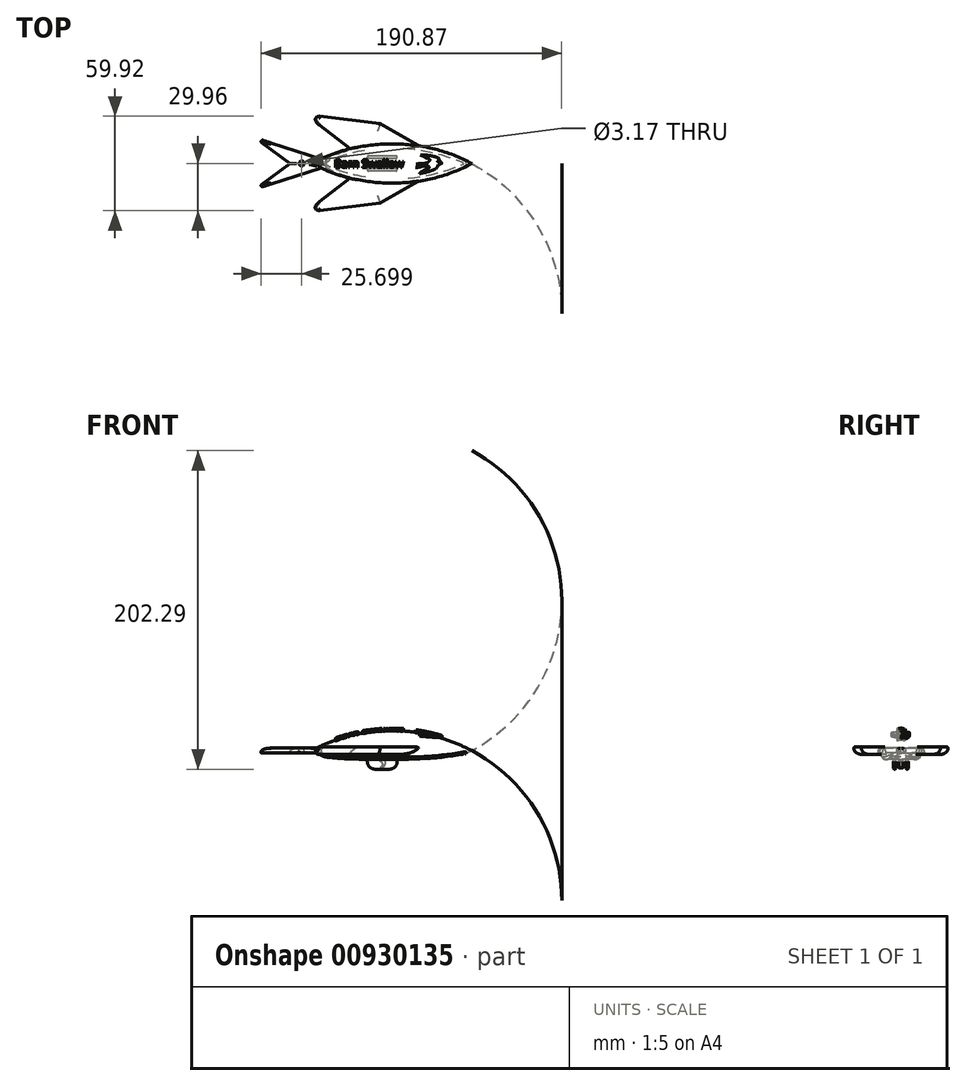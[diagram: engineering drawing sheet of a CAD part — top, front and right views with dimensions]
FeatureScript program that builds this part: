
annotation { "Feature Type Name" : "Feature", "Feature Type Description" : "" }
export const myFeature = defineFeature(function(context is Context, id is Id, definition is map)
    precondition{}
    {
        {
            var Q0;
            Q0=qCreatedBy(makeId("Top.planeOp"),FACE);
            var sketch = newSketch(context, id + "F0", { "sketchPlane" : qUnion([Q0])});
            skArc(sketch, "E0", {"start": v(50.5, 0) * mm, "mid": v(-0.3, 12.7) * mm, "end": v(-51.1, 0) * mm});
            skLineSegment(sketch, "E1", {"start": v(-51.1, 0) * mm, "end": v(50.5, 0) * mm});
            skSolve(sketch);
        }
        {
            var Q0;
            Q0 = qSketchRegion(id + "F0", true);
            var Q1;
            Q1=sQuery(id+"F0.wireOp",EDGE,"E1");
            revolve(context, id + "F1", {"surfaceOperationType" : NewSurfaceOperationType.NEW, "entities" : qUnion([Q0]), "axis" : qUnion([Q1]), "revolveType" : RevolveType.FULL});
        }
        {
            var Q0;
            Q0=qCreatedBy(makeId("Top.planeOp"),FACE);
            var sketch = newSketch(context, id + "F2", { "sketchPlane" : qUnion([Q0])});
            skLineSegment(sketch, "E2", {"start": v(25.4, 6.35) * mm, "end": v(-7.66, 25.44) * mm});
            skLineSegment(sketch, "E3", {"start": v(-7.66, 25.44) * mm, "end": v(-58.1, 31.57) * mm});
            skLineSegment(sketch, "E4", {"start": v(-25.4, 6.35) * mm, "end": v(25.4, 6.35) * mm});
            skPoint(sketch, "E5.visualSharp", {"position": v(-7.66, 25.44) * mm});
            skLineSegment(sketch, "E6", {"start": v(-12.7, 0) * mm, "end": v(12.7, 0) * mm, "construction": true});
            skLineSegment(sketch, "E7.MirrorCS", {"start": v(-7.66, -25.44) * mm, "end": v(-7.66, -25.44) * mm});
            skPoint(sketch, "E8.MirrorP", {"position": v(-7.66, -25.44) * mm});
            skLineSegment(sketch, "E9.MirrorCS", {"start": v(-25.4, -6.35) * mm, "end": v(25.4, -6.35) * mm});
            skLineSegment(sketch, "E10.MirrorCS", {"start": v(-7.66, -25.44) * mm, "end": v(-58.1, -31.57) * mm});
            skLineSegment(sketch, "E11.MirrorCS", {"start": v(25.4, -6.35) * mm, "end": v(-7.66, -25.44) * mm});
            skLineSegment(sketch, "E12", {"start": v(-25.4, 6.35) * mm, "end": v(-58.1, 31.57) * mm});
            skLineSegment(sketch, "E13", {"start": v(-58.1, -31.57) * mm, "end": v(-25.4, -6.35) * mm});
            skSolve(sketch);
        }
        {
            var Q0;
            Q0 = qSketchRegion(id + "F2", true);
            extrude(context, id + "F3", {"entities" : qUnion([Q0]), "operationType" : NewBodyOperationType.ADD, "depth" : 4.7 * mm, "offsetDistance" : 25.4 * mm, "symmetric" : true});
        }
        {
            var Q0;
            Q0=qCreatedBy(makeId("Front.planeOp"),FACE);
            var sketch = newSketch(context, id + "F4", { "sketchPlane" : qUnion([Q0])});
            skLineSegment(sketch, "E14", {"start": v(-65.9, -0.5) * mm, "end": v(22.2, 2.57) * mm});
            skLineSegment(sketch, "E15", {"start": v(22.2, 2.57) * mm, "end": v(19.39, 14.95) * mm});
            skLineSegment(sketch, "E16", {"start": v(19.39, 14.95) * mm, "end": v(-60.79, 12.82) * mm});
            skLineSegment(sketch, "E17", {"start": v(-60.79, 12.82) * mm, "end": v(-65.9, -0.5) * mm});
            skLineSegment(sketch, "E18", {"start": v(13.47, 0) * mm, "end": v(-58.08, 0) * mm, "construction": true});
            skSolve(sketch);
        }
        {
            var Q0;
            Q0=makeQuery(id+"F3.opExtrude","CAP_EDGE",EDGE,{"disambiguationData":[OSD([sQuery(id+"F2.wireOp",EDGE,"E2")])],"isStart":true});
            var Q1;
            Q1=makeQuery(id+"F3.opExtrude","CAP_EDGE",EDGE,{"disambiguationData":[OSD([sQuery(id+"F2.wireOp",EDGE,"E3")])],"isStart":true});
            var Q2;
            Q2=makeQuery(id+"F3.opExtrude","CAP_EDGE",EDGE,{"disambiguationData":[OSD([sQuery(id+"F2.wireOp",EDGE,"E11.MirrorCS")])],"isStart":true});
            var Q3;
            Q3=makeQuery(id+"F3.opExtrude","CAP_EDGE",EDGE,{"disambiguationData":[OSD([sQuery(id+"F2.wireOp",EDGE,"E10.MirrorCS")])],"isStart":true});
            fillet(context, id + "F5", {"entities" : qUnion([Q0, Q1, Q2, Q3]), "radius" : 5.08 * mm, "tangentPropagation" : true, "allowEdgeOverflow" : false});
        }
        {
            var Q0;
            Q0=makeQuery(id+"F3.opExtrude","CAP_EDGE",EDGE,{"disambiguationData":[OSD([sQuery(id+"F2.wireOp",EDGE,"E12")])],"isStart":false});
            var Q1;
            Q1=makeQuery(id+"F3.opExtrude","CAP_EDGE",EDGE,{"disambiguationData":[OSD([sQuery(id+"F2.wireOp",EDGE,"E13")])],"isStart":false});
            chamfer(context, id + "F6", {"entities" : qUnion([Q0, Q1]), "width" : 5.08 * mm, "tangentPropagation" : true});
        }
        {
            var Q0;
            Q0=qCreatedBy(makeId("Front.planeOp"),FACE);
            var sketch = newSketch(context, id + "F7", { "sketchPlane" : qUnion([Q0])});
            skLineSegment(sketch, "E19", {"start": v(6.9, -5.44) * mm, "end": v(-17.13, -5.44) * mm});
            skLineSegment(sketch, "E20", {"start": v(54.85, -5.44) * mm, "end": v(0, -26.45) * mm});
            skLineSegment(sketch, "E21", {"start": v(0, -26.45) * mm, "end": v(-69.23, -5.44) * mm});
            skLineSegment(sketch, "E22", {"start": v(58.81, 0) * mm, "end": v(73.58, 4.5) * mm});
            skLineSegment(sketch, "E23", {"start": v(58.81, 0) * mm, "end": v(54.85, -5.44) * mm});
            skLineSegment(sketch, "E24", {"start": v(-63.97, -0.59) * mm, "end": v(-66.78, 0) * mm});
            skLineSegment(sketch, "E25", {"start": v(-66.78, 0) * mm, "end": v(-69.23, -5.44) * mm});
            skPoint(sketch, "E26.visualSharp", {"position": v(40.98, -5.44) * mm});
            skArc(sketch, "E26.filletArc", {"start": v(6.9, -5.44) * mm, "mid": v(40.6, -2.94) * mm, "end": v(73.58, 4.5) * mm});
            skPoint(sketch, "E27.visualSharp", {"position": v(-40.8, -5.44) * mm});
            skArc(sketch, "E27.filletArc", {"start": v(-63.97, -0.59) * mm, "mid": v(-40.67, -4.22) * mm, "end": v(-17.13, -5.44) * mm});
            skSolve(sketch);
        }
        {
            var Q0;
            Q0 = qSketchRegion(id + "F7", true);
            extrude(context, id + "F8", {"entities" : qUnion([Q0]), "operationType" : NewBodyOperationType.REMOVE, "oppositeDirection" : true, "depth" : 25.4 * mm, "offsetDistance" : 25.4 * mm, "symmetric" : true});
        }
        {
            var Q0;
            Q0=makeQuery(id+"F8.boolean.opBoolean","INTERSECT",EDGE,{"derivedFrom":[makeQuery(id+"F1.opRevolve","SWEPT_FACE",FACE,{"disambiguationData":[OSD([sQuery(id+"F0.wireOp",EDGE,"E0")])]}),makeQuery(id+"F8.opExtrude","SWEPT_FACE",FACE,{"disambiguationData":[OSD([sQuery(id+"F7.wireOp",EDGE,"E19")])]})]});
            fillet(context, id + "F9", {"entities" : qUnion([Q0]), "radius" : 2.03 * mm, "tangentPropagation" : true, "allowEdgeOverflow" : false});
        }
        {
            var Q0;
            Q0=qCreatedBy(makeId("Top.planeOp"),FACE);
            var sketch = newSketch(context, id + "F10", { "sketchPlane" : qUnion([Q0])});
            skLineSegment(sketch, "E28", {"start": v(-36.1, 0) * mm, "end": v(-86.74, 16.16) * mm});
            skLineSegment(sketch, "E29", {"start": v(-86.74, 16.16) * mm, "end": v(-64.97, 0) * mm});
            skLineSegment(sketch, "E30", {"start": v(-64.97, 0) * mm, "end": v(-36.1, 0) * mm});
            skLineSegment(sketch, "E31.MirrorCS", {"start": v(-86.74, -16.16) * mm, "end": v(-64.97, 0) * mm});
            skLineSegment(sketch, "E32.MirrorCS", {"start": v(-36.1, 0) * mm, "end": v(-86.74, -16.16) * mm});
            skSolve(sketch);
        }
        {
            var Q0;
            Q0 = qSketchRegion(id + "F10", true);
            extrude(context, id + "F11", {"entities" : qUnion([Q0]), "operationType" : NewBodyOperationType.ADD, "depth" : 3.17 * mm, "offsetDistance" : 25.4 * mm, "symmetric" : true});
        }
        {
            var Q0;
            Q0=makeQuery(id+"F11.opExtrude","CAP_EDGE",EDGE,{"disambiguationData":[OSD([sQuery(id+"F10.wireOp",EDGE,"E29")])],"isStart":false});
            var Q1;
            Q1=makeQuery(id+"F11.opExtrude","CAP_EDGE",EDGE,{"disambiguationData":[OSD([sQuery(id+"F10.wireOp",EDGE,"E31.MirrorCS")])],"isStart":false});
            fillet(context, id + "F12", {"entities" : qUnion([Q0, Q1]), "radius" : 2.54 * mm, "tangentPropagation" : true, "allowEdgeOverflow" : false});
        }
        {
            var Q0;
            Q0=makeQuery(id+"F8.boolean.opBoolean","COPY",FACE,{"derivedFrom":makeQuery(id+"F8.opExtrude","SWEPT_FACE",FACE,{"disambiguationData":[OSD([sQuery(id+"F7.wireOp",EDGE,"E19")])]})});
            var sketch = newSketch(context, id + "F13", { "sketchPlane" : qUnion([Q0])});
            skLineSegment(sketch, "E33", {"start": v(6.9, 9.85) * mm, "end": v(-17.13, -8.68) * mm, "construction": true});
            skLineSegment(sketch, "E34", {"start": v(-17.13, 8.68) * mm, "end": v(6.9, -9.85) * mm, "construction": true});
            skLineSegment(sketch, "E35.bottom", {"start": v(-4.17, 1.32) * mm, "end": v(-7.59, 1.32) * mm});
            skLineSegment(sketch, "E35.top", {"start": v(-4.17, -1.32) * mm, "end": v(-7.59, -1.32) * mm});
            skLineSegment(sketch, "E35.left", {"start": v(-4.17, 1.32) * mm, "end": v(-4.17, -1.32) * mm});
            skLineSegment(sketch, "E35.right", {"start": v(-7.59, 1.32) * mm, "end": v(-7.59, -1.32) * mm});
            skPoint(sketch, "E35.middle", {"position": v(-5.88, 0) * mm});
            skSolve(sketch);
        }
        {
            var Q0;
            Q0=makeQuery(id+"F13.imprint","IMPRINT",FACE,{"disambiguationData":[TD([[makeQuery(id+"F13.imprint","IMPRINT",EDGE,{"derivedFrom":sQuery(id+"F13.wireOp",EDGE,"E35.bottom")}),1.0]])]});
            var Q1;
            Q1=sQuery(id+"F13.wireOp",EDGE,"E35.right");
            var Q2;
            Q2=sQuery(id+"F13.wireOp",EDGE,"E35.bottom");
            var Q3;
            Q3=sQuery(id+"F13.wireOp",EDGE,"E35.left");
            var Q4;
            Q4=sQuery(id+"F13.wireOp",EDGE,"E35.top");
            extrude(context, id + "F14", {"entities" : qUnion([Q0]), "operationType" : NewBodyOperationType.ADD, "surfaceEntities" : qUnion([Q1, Q2, Q3, Q4]), "depth" : 6.35 * mm, "offsetDistance" : 25.4 * mm});
        }
        {
            var Q0;
            Q0=makeQuery(id+"F14.opExtrude","SWEPT_FACE",FACE,{"disambiguationData":[OSD([sQuery(id+"F13.wireOp",EDGE,"E35.bottom")])]});
            var sketch = newSketch(context, id + "F15", { "sketchPlane" : qUnion([Q0])});
            skCircle(sketch, "E36", {"center": v(-7.59, -8.61) * mm, "radius": 1.59 * mm});
            skSolve(sketch);
        }
        {
            var Q0;
            {var subQ0=sQuery(id+"F15.wireOp",EDGE,"E36");var subQ1=makeQuery(id+"F14.opExtrude","SWEPT_EDGE",EDGE,{"disambiguationData":[OSD([sQuery(id+"F13.wireOp",EDGE,"E35.bottom"),sQuery(id+"F13.wireOp",EDGE,"E35.right")])]});var subQ2=makeQuery(id+"F15.imprint","INTERSECT",VERTEX,{"disambiguationData":[OD(0.0)],"derivedFrom":[subQ1,subQ0]});Q0=makeQuery(id+"F15.imprint","IMPRINT",FACE,{"disambiguationData":[TD([[makeQuery(id+"F15.imprint","IMPRINT",EDGE,{"disambiguationData":[TD([[subQ2,-1.0]])],"derivedFrom":subQ0}),1.0]])]});}
            extrude(context, id + "F16", {"entities" : qUnion([Q0]), "operationType" : NewBodyOperationType.REMOVE, "oppositeDirection" : true, "depth" : 25.4 * mm, "offsetDistance" : 25.4 * mm, "symmetric" : true});
        }
        {
            var Q0;
            Q0=makeQuery(id+"F14.opExtrude","CAP_EDGE",EDGE,{"disambiguationData":[OSD([sQuery(id+"F13.wireOp",EDGE,"E35.left")])],"isStart":false});
            fillet(context, id + "F17", {"entities" : qUnion([Q0]), "radius" : 5.08 * mm, "tangentPropagation" : true, "allowEdgeOverflow" : false});
        }
        {
            var Q0;
            {var subQ0=sQuery(id+"F13.wireOp",EDGE,"E35.bottom");var subQ1=sQuery(id+"F13.wireOp",EDGE,"E35.right");var subQ2=sQuery(id+"F13.wireOp",EDGE,"E35.left");var subQ3=sQuery(id+"F13.wireOp",EDGE,"E35.top");Q0=makeQuery(id+"F17.opFillet","BLEND_EDGE",EDGE,{"blendedFrom":[makeQuery(id+"F14.opExtrude","CAP_EDGE",EDGE,{"disambiguationData":[OSD([subQ2])],"isStart":false}),makeQuery(id+"F16.boolean.opBoolean","SPLIT",FACE,{"disambiguationData":[TD([makeQuery(id+"F14.opExtrude","CAP_FACE",FACE,{"disambiguationData":[OSD([subQ0,subQ3,subQ2,subQ1])],"isStart":false})])],"derivedFrom":makeQuery(id+"F14.opExtrude","SWEPT_FACE",FACE,{"disambiguationData":[OSD([subQ1])]})})],"blendedInto":[makeQuery(id+"F16.boolean.opBoolean","SPLIT",FACE,{"disambiguationData":[TD([makeQuery(id+"F14.opExtrude","CAP_FACE",FACE,{"disambiguationData":[OSD([subQ0,subQ3,subQ2,subQ1])],"isStart":false})])],"derivedFrom":makeQuery(id+"F14.opExtrude","SWEPT_FACE",FACE,{"disambiguationData":[OSD([subQ1])]})})]});}
            fillet(context, id + "F18", {"entities" : qUnion([Q0]), "radius" : 1.27 * mm, "tangentPropagation" : true, "allowEdgeOverflow" : false});
        }
        {
            var Q0;
            Q0=makeQuery(id+"F11.opExtrude","CAP_FACE",FACE,{"disambiguationData":[OSD([sQuery(id+"F10.wireOp",EDGE,"E28"),sQuery(id+"F10.wireOp",EDGE,"E29"),sQuery(id+"F10.wireOp",EDGE,"E31.MirrorCS"),sQuery(id+"F10.wireOp",EDGE,"E32.MirrorCS")])],"isStart":false});
            var sketch = newSketch(context, id + "F19", { "sketchPlane" : qUnion([Q0])});
            skCircle(sketch, "E37", {"center": v(-57.53, 0) * mm, "radius": 1.59 * mm});
            skSolve(sketch);
        }
        {
            var Q0;
            Q0 = qSketchRegion(id + "F19", true);
            extrude(context, id + "F20", {"entities" : qUnion([Q0]), "operationType" : NewBodyOperationType.REMOVE, "oppositeDirection" : true, "depth" : 25.4 * mm, "offsetDistance" : 25.4 * mm});
        }
        {
            var Q0;
            Q0=makeQuery(id+"F20.boolean.opBoolean","COPY",EDGE,{"derivedFrom":makeQuery(id+"F20.opExtrude","CAP_EDGE",EDGE,{"disambiguationData":[OSD([sQuery(id+"F19.wireOp",EDGE,"E37")])],"isStart":true})});
            var Q1;
            Q1=makeQuery(id+"F20.boolean.opBoolean","INTERSECT",EDGE,{"derivedFrom":[makeQuery(id+"F11.opExtrude","CAP_FACE",FACE,{"disambiguationData":[OSD([sQuery(id+"F10.wireOp",EDGE,"E28"),sQuery(id+"F10.wireOp",EDGE,"E29"),sQuery(id+"F10.wireOp",EDGE,"E31.MirrorCS"),sQuery(id+"F10.wireOp",EDGE,"E32.MirrorCS")])],"isStart":true}),makeQuery(id+"F20.opExtrude","SWEPT_FACE",FACE,{"disambiguationData":[OSD([sQuery(id+"F19.wireOp",EDGE,"E37")])]})]});
            fillet(context, id + "F21", {"entities" : qUnion([Q0, Q1]), "radius" : 1.27 * mm, "tangentPropagation" : true, "allowEdgeOverflow" : false});
        }
        {
            var Q0;
            Q0=qCreatedBy(makeId("Top.planeOp"),FACE);
            var sketch = newSketch(context, id + "F22", { "sketchPlane" : qUnion([Q0])});
            skArc(sketch, "E38", {"start": v(28.55, 3.87) * mm, "mid": v(23.4, 5.07) * mm, "end": v(18.1, 5.23) * mm});
            skArc(sketch, "E39", {"start": v(28.55, 1.44) * mm, "mid": v(29.73, 2.66) * mm, "end": v(28.55, 3.87) * mm});
            skArc(sketch, "E40", {"start": v(31.03, 0.49) * mm, "mid": v(30.84, 1.08) * mm, "end": v(30.27, 1.34) * mm});
            skLineSegment(sketch, "E41", {"start": v(31.03, 0.49) * mm, "end": v(31.75, 0.2) * mm});
            skLineSegment(sketch, "E42", {"start": v(31.75, 0.2) * mm, "end": v(31.06, 0) * mm});
            skArc(sketch, "E43", {"start": v(29.06, -0.78) * mm, "mid": v(30.1, -0.51) * mm, "end": v(31.06, 0) * mm});
            skArc(sketch, "E44", {"start": v(27.23, -3.56) * mm, "mid": v(28.5, -2.4) * mm, "end": v(29.06, -0.78) * mm});
            skArc(sketch, "E45", {"start": v(17.18, -6.38) * mm, "mid": v(22.3, -5.33) * mm, "end": v(27.23, -3.56) * mm});
            skArc(sketch, "E46", {"start": v(23.34, -2.75) * mm, "mid": v(20.12, -4.34) * mm, "end": v(17.18, -6.38) * mm});
            skArc(sketch, "E47", {"start": v(23.34, -2.75) * mm, "mid": v(23.32, -1.97) * mm, "end": v(22.63, -1.59) * mm});
            skArc(sketch, "E48", {"start": v(22.63, -1.59) * mm, "mid": v(20.81, -1.57) * mm, "end": v(19.01, -1.84) * mm});
            skArc(sketch, "E49", {"start": v(14.88, -2.63) * mm, "mid": v(16.97, -2.34) * mm, "end": v(19.01, -1.84) * mm});
            skArc(sketch, "E50", {"start": v(14.88, -2.63) * mm, "mid": v(16.51, -2.18) * mm, "end": v(18.1, -1.59) * mm});
            skArc(sketch, "E51", {"start": v(18.1, -1.59) * mm, "mid": v(18.5, -1.13) * mm, "end": v(18.23, -0.59) * mm});
            skArc(sketch, "E52", {"start": v(18.23, -0.59) * mm, "mid": v(16.72, -0.48) * mm, "end": v(15.2, -0.43) * mm});
            skArc(sketch, "E53", {"start": v(18.23, 0) * mm, "mid": v(16.71, -0.15) * mm, "end": v(15.2, -0.43) * mm});
            skArc(sketch, "E54", {"start": v(18.23, 0) * mm, "mid": v(19.73, 0) * mm, "end": v(21.22, 0.2) * mm});
            skArc(sketch, "E55", {"start": v(21.22, 0.2) * mm, "mid": v(22.34, 0.6) * mm, "end": v(23.34, 1.23) * mm});
            skArc(sketch, "E56", {"start": v(23.34, 1.23) * mm, "mid": v(23.67, 1.87) * mm, "end": v(23.9, 2.54) * mm});
            skArc(sketch, "E57", {"start": v(30.27, 1.34) * mm, "mid": v(29.73, 1.33) * mm, "end": v(29.2, 1.28) * mm});
            skArc(sketch, "E58", {"start": v(28.55, 1.44) * mm, "mid": v(28.86, 1.3) * mm, "end": v(29.2, 1.28) * mm});
            skArc(sketch, "E59", {"start": v(23.9, 2.54) * mm, "mid": v(22.79, 3.21) * mm, "end": v(21.52, 3.53) * mm});
            skArc(sketch, "E60", {"start": v(21.52, 3.53) * mm, "mid": v(19.87, 4.5) * mm, "end": v(18.1, 5.23) * mm});
            skSolve(sketch);
        }
        {
            var Q0;
            Q0 = qSketchRegion(id + "F22", true);
            extrude(context, id + "F23", {"entities" : qUnion([Q0]), "operationType" : NewBodyOperationType.ADD, "depth" : 25.4 * mm, "offsetDistance" : 25.4 * mm});
        }
        {
            var Q0;
            Q0=qCreatedBy(makeId("Front.planeOp"),FACE);
            var sketch = newSketch(context, id + "F24", { "sketchPlane" : qUnion([Q0])});
            skArc(sketch, "E61", {"start": v(52.15, 1.07) * mm, "mid": v(0.1, 14.29) * mm, "end": v(-51.93, 1.08) * mm});
            skLineSegment(sketch, "E62", {"start": v(52.15, 34.59) * mm, "end": v(-51.93, 34.59) * mm});
            skLineSegment(sketch, "E63", {"start": v(-53.87, 0) * mm, "end": v(54.08, 0) * mm, "construction": true});
            skLineSegment(sketch, "E64", {"start": v(52.15, 34.59) * mm, "end": v(52.15, 1.07) * mm});
            skLineSegment(sketch, "E65", {"start": v(-51.93, 34.59) * mm, "end": v(-51.93, 1.08) * mm});
            skSolve(sketch);
        }
        {
            var Q0;
            Q0=qCreatedBy(makeId("Top.planeOp"),FACE);
            var sketch = newSketch(context, id + "F25", { "sketchPlane" : qUnion([Q0])});
            skText(sketch, "E66", { "text": "Barn Swallow ", "fontName": "OpenSans-Regular.ttf"});
            skLineSegment(sketch, "E67", {"start": v(7.68, 0) * mm, "end": v(-36.77, 0) * mm, "construction": true});
            const initialGuessF25  = {"E66": [-0.03677, -0.00254, 1, 0, 0.00507]};
            skSetInitialGuess(sketch, initialGuessF25);
            skSolve(sketch);
        }
        {
            var Q0;
            Q0 = qSketchRegion(id + "F25", true);
            extrude(context, id + "F26", {"entities" : qUnion([Q0]), "operationType" : NewBodyOperationType.ADD, "depth" : 25.4 * mm, "offsetDistance" : 25.4 * mm});
        }
        {
            var Q0;
            Q0=makeQuery(id+"F24.imprint","IMPRINT",FACE,{"disambiguationData":[TD([[makeQuery(id+"F24.imprint","IMPRINT",EDGE,{"derivedFrom":sQuery(id+"F24.wireOp",EDGE,"E61")}),-1.0]])]});
            var Q1;
            Q1=sQuery(id+"F24.wireOp",EDGE,"E63");
            revolve(context, id + "F27", {"operationType" : NewBodyOperationType.REMOVE, "surfaceOperationType" : NewSurfaceOperationType.NEW, "entities" : qUnion([Q0]), "axis" : qUnion([Q1]), "revolveType" : RevolveType.SYMMETRIC, "oppositeDirection" : true, "angle" : 60 * degree});
        }
        {
            var Q0;
            Q0=makeQuery(id+"F8.boolean.opBoolean","COPY",FACE,{"derivedFrom":makeQuery(id+"F8.opExtrude","SWEPT_FACE",FACE,{"disambiguationData":[OSD([sQuery(id+"F7.wireOp",EDGE,"E19")])]})});
            var sketch = newSketch(context, id + "F28", { "sketchPlane" : qUnion([Q0])});
            skLineSegment(sketch, "E68.bottom", {"start": v(3.17, 3.18) * mm, "end": v(-15.88, 3.17) * mm});
            skLineSegment(sketch, "E68.top", {"start": v(3.17, 4.76) * mm, "end": v(-15.88, 4.76) * mm});
            skLineSegment(sketch, "E68.left", {"start": v(3.17, 3.18) * mm, "end": v(3.17, 4.76) * mm});
            skLineSegment(sketch, "E68.right", {"start": v(-15.88, 3.17) * mm, "end": v(-15.88, 4.76) * mm});
            skLineSegment(sketch, "E69.MirrorCS", {"start": v(3.17, -3.18) * mm, "end": v(-15.88, -3.17) * mm});
            skLineSegment(sketch, "E70.MirrorCS", {"start": v(-15.88, -3.17) * mm, "end": v(-15.88, -4.76) * mm});
            skLineSegment(sketch, "E71.MirrorCS", {"start": v(3.17, -4.76) * mm, "end": v(-15.88, -4.76) * mm});
            skLineSegment(sketch, "E72.MirrorCS", {"start": v(3.17, -3.18) * mm, "end": v(3.17, -4.76) * mm});
            skSolve(sketch);
        }
        {
            var Q0;
            Q0 = qSketchRegion(id + "F28", true);
            extrude(context, id + "F29", {"entities" : qUnion([Q0]), "operationType" : NewBodyOperationType.ADD, "depth" : 6.35 * mm, "offsetDistance" : 25.4 * mm});
        }
        {
            var Q0;
            Q0=makeQuery(id+"F29.opExtrude","CAP_EDGE",EDGE,{"disambiguationData":[OSD([sQuery(id+"F28.wireOp",EDGE,"E68.left")])],"isStart":false});
            var Q1;
            Q1=makeQuery(id+"F29.opExtrude","CAP_EDGE",EDGE,{"disambiguationData":[OSD([sQuery(id+"F28.wireOp",EDGE,"E72.MirrorCS")])],"isStart":false});
            var Q2;
            Q2=makeQuery(id+"F29.opExtrude","CAP_EDGE",EDGE,{"disambiguationData":[OSD([sQuery(id+"F28.wireOp",EDGE,"E68.right")])],"isStart":false});
            var Q3;
            Q3=makeQuery(id+"F29.opExtrude","CAP_EDGE",EDGE,{"disambiguationData":[OSD([sQuery(id+"F28.wireOp",EDGE,"E70.MirrorCS")])],"isStart":false});
            fillet(context, id + "F30", {"entities" : qUnion([Q0, Q1, Q2, Q3]), "radius" : 5.08 * mm, "tangentPropagation" : true, "allowEdgeOverflow" : false});
        }
        {
            var Q0;
            Q0=makeQuery(id+"F29.opExtrude","CAP_EDGE",EDGE,{"disambiguationData":[OSD([sQuery(id+"F28.wireOp",EDGE,"E68.top")])],"isStart":false});
            var Q1;
            Q1=makeQuery(id+"F29.opExtrude","CAP_EDGE",EDGE,{"disambiguationData":[OSD([sQuery(id+"F28.wireOp",EDGE,"E69.MirrorCS")])],"isStart":false});
            var Q2;
            Q2=makeQuery(id+"F29.opExtrude","CAP_EDGE",EDGE,{"disambiguationData":[OSD([sQuery(id+"F28.wireOp",EDGE,"E68.bottom")])],"isStart":false});
            var Q3;
            Q3=makeQuery(id+"F29.opExtrude","CAP_EDGE",EDGE,{"disambiguationData":[OSD([sQuery(id+"F28.wireOp",EDGE,"E71.MirrorCS")])],"isStart":false});
            var Q4;
            Q4=makeQuery(id+"F16.boolean.opBoolean","INTERSECT",EDGE,{"derivedFrom":[makeQuery(id+"F14.opExtrude","SWEPT_FACE",FACE,{"disambiguationData":[OSD([sQuery(id+"F13.wireOp",EDGE,"E35.bottom")])]}),makeQuery(id+"F16.opExtrude","SWEPT_FACE",FACE,{"disambiguationData":[OSD([sQuery(id+"F15.wireOp",EDGE,"E36")])]})]});
            var Q5;
            Q5=makeQuery(id+"F16.boolean.opBoolean","INTERSECT",EDGE,{"derivedFrom":[makeQuery(id+"F14.opExtrude","SWEPT_FACE",FACE,{"disambiguationData":[OSD([sQuery(id+"F13.wireOp",EDGE,"E35.top")])]}),makeQuery(id+"F16.opExtrude","SWEPT_FACE",FACE,{"disambiguationData":[OSD([sQuery(id+"F15.wireOp",EDGE,"E36")])]})]});
            var Q6;
            {var subQ0=sQuery(id+"F15.wireOp",EDGE,"E36");var subQ1=sQuery(id+"F13.wireOp",EDGE,"E35.right");var subQ2=sQuery(id+"F13.wireOp",EDGE,"E35.bottom");Q6=makeQuery(id+"F16.boolean.opBoolean","COPY",EDGE,{"derivedFrom":makeQuery(id+"F16.opExtrude","SWEPT_EDGE",EDGE,{"disambiguationData":[OSD([subQ2,subQ1,subQ0]),TDD([makeQuery(id+"F15.imprint","INTERSECT",VERTEX,{"disambiguationData":[OD(1.0)],"derivedFrom":[makeQuery(id+"F14.opExtrude","SWEPT_EDGE",EDGE,{"disambiguationData":[OSD([subQ2,subQ1])]}),subQ0]})])]})});}
            var Q7;
            {var subQ0=sQuery(id+"F13.wireOp",EDGE,"E35.bottom");var subQ1=sQuery(id+"F13.wireOp",EDGE,"E35.right");Q7=makeQuery(id+"F16.boolean.opBoolean","SPLIT",EDGE,{"disambiguationData":[TD([makeQuery(id+"F8.boolean.opBoolean","COPY",FACE,{"derivedFrom":makeQuery(id+"F8.opExtrude","SWEPT_FACE",FACE,{"disambiguationData":[OSD([sQuery(id+"F7.wireOp",EDGE,"E19")])]})})])],"derivedFrom":makeQuery(id+"F14.opExtrude","SWEPT_EDGE",EDGE,{"disambiguationData":[OSD([subQ0,subQ1])]})});}
            var Q8;
            {var subQ0=sQuery(id+"F13.wireOp",EDGE,"E35.top");var subQ1=sQuery(id+"F13.wireOp",EDGE,"E35.right");Q8=makeQuery(id+"F16.boolean.opBoolean","SPLIT",EDGE,{"disambiguationData":[TD([makeQuery(id+"F8.boolean.opBoolean","COPY",FACE,{"derivedFrom":makeQuery(id+"F8.opExtrude","SWEPT_FACE",FACE,{"disambiguationData":[OSD([sQuery(id+"F7.wireOp",EDGE,"E19")])]})})])],"derivedFrom":makeQuery(id+"F14.opExtrude","SWEPT_EDGE",EDGE,{"disambiguationData":[OSD([subQ0,subQ1])]})});}
            var Q9;
            {var subQ0=sQuery(id+"F2.wireOp",EDGE,"E10.MirrorCS");Q9=makeQuery(id+"F5.opFillet","BLEND_EDGE",EDGE,{"blendedFrom":[makeQuery(id+"F3.opExtrude","CAP_EDGE",EDGE,{"disambiguationData":[OSD([subQ0])],"isStart":true}),makeQuery(id+"F3.opExtrude","CAP_FACE",FACE,{"disambiguationData":[OSD([sQuery(id+"F2.wireOp",EDGE,"E9.MirrorCS"),subQ0,sQuery(id+"F2.wireOp",EDGE,"E11.MirrorCS"),sQuery(id+"F2.wireOp",EDGE,"E13")])],"isStart":false})],"blendedInto":[makeQuery(id+"F3.opExtrude","CAP_FACE",FACE,{"disambiguationData":[OSD([sQuery(id+"F2.wireOp",EDGE,"E9.MirrorCS"),subQ0,sQuery(id+"F2.wireOp",EDGE,"E11.MirrorCS"),sQuery(id+"F2.wireOp",EDGE,"E13")])],"isStart":false})]});}
            var Q10;
            {var subQ0=sQuery(id+"F2.wireOp",EDGE,"E11.MirrorCS");Q10=makeQuery(id+"F5.opFillet","BLEND_EDGE",EDGE,{"blendedFrom":[makeQuery(id+"F3.opExtrude","CAP_EDGE",EDGE,{"disambiguationData":[OSD([subQ0])],"isStart":true}),makeQuery(id+"F3.opExtrude","CAP_FACE",FACE,{"disambiguationData":[OSD([sQuery(id+"F2.wireOp",EDGE,"E9.MirrorCS"),sQuery(id+"F2.wireOp",EDGE,"E10.MirrorCS"),subQ0,sQuery(id+"F2.wireOp",EDGE,"E13")])],"isStart":false})],"blendedInto":[makeQuery(id+"F3.opExtrude","CAP_FACE",FACE,{"disambiguationData":[OSD([sQuery(id+"F2.wireOp",EDGE,"E9.MirrorCS"),sQuery(id+"F2.wireOp",EDGE,"E10.MirrorCS"),subQ0,sQuery(id+"F2.wireOp",EDGE,"E13")])],"isStart":false})]});}
            var Q11;
            {var subQ0=sQuery(id+"F2.wireOp",EDGE,"E13");Q11=makeQuery(id+"F6.opChamfer","BLEND_EDGE",EDGE,{"blendedFrom":[makeQuery(id+"F3.opExtrude","CAP_EDGE",EDGE,{"disambiguationData":[OSD([subQ0])],"isStart":false}),makeQuery(id+"F3.opExtrude","CAP_FACE",FACE,{"disambiguationData":[OSD([sQuery(id+"F2.wireOp",EDGE,"E9.MirrorCS"),sQuery(id+"F2.wireOp",EDGE,"E10.MirrorCS"),sQuery(id+"F2.wireOp",EDGE,"E11.MirrorCS"),subQ0])],"isStart":false})],"blendedInto":[makeQuery(id+"F3.opExtrude","CAP_FACE",FACE,{"disambiguationData":[OSD([sQuery(id+"F2.wireOp",EDGE,"E9.MirrorCS"),sQuery(id+"F2.wireOp",EDGE,"E10.MirrorCS"),sQuery(id+"F2.wireOp",EDGE,"E11.MirrorCS"),subQ0])],"isStart":false})]});}
            var Q12;
            {var subQ0=sQuery(id+"F2.wireOp",EDGE,"E13");Q12=makeQuery(id+"F6.opChamfer","BLEND_EDGE",EDGE,{"blendedFrom":[makeQuery(id+"F3.opExtrude","CAP_EDGE",EDGE,{"disambiguationData":[OSD([subQ0])],"isStart":false}),makeQuery(id+"F3.opExtrude","CAP_FACE",FACE,{"disambiguationData":[OSD([sQuery(id+"F2.wireOp",EDGE,"E9.MirrorCS"),sQuery(id+"F2.wireOp",EDGE,"E10.MirrorCS"),sQuery(id+"F2.wireOp",EDGE,"E11.MirrorCS"),subQ0])],"isStart":true})],"blendedInto":[makeQuery(id+"F3.opExtrude","CAP_FACE",FACE,{"disambiguationData":[OSD([sQuery(id+"F2.wireOp",EDGE,"E9.MirrorCS"),sQuery(id+"F2.wireOp",EDGE,"E10.MirrorCS"),sQuery(id+"F2.wireOp",EDGE,"E11.MirrorCS"),subQ0])],"isStart":true})]});}
            var Q13;
            Q13=makeQuery(id+"F11.opExtrude","CAP_EDGE",EDGE,{"disambiguationData":[OSD([sQuery(id+"F10.wireOp",EDGE,"E32.MirrorCS")])],"isStart":false});
            var Q14;
            Q14=makeQuery(id+"F11.opExtrude","CAP_EDGE",EDGE,{"disambiguationData":[OSD([sQuery(id+"F10.wireOp",EDGE,"E31.MirrorCS")])],"isStart":true});
            var Q15;
            Q15=makeQuery(id+"F11.opExtrude","CAP_EDGE",EDGE,{"disambiguationData":[OSD([sQuery(id+"F10.wireOp",EDGE,"E29")])],"isStart":true});
            var Q16;
            Q16=makeQuery(id+"F11.opExtrude","CAP_EDGE",EDGE,{"disambiguationData":[OSD([sQuery(id+"F10.wireOp",EDGE,"E28")])],"isStart":false});
            var Q17;
            {var subQ0=sQuery(id+"F2.wireOp",EDGE,"E2");Q17=makeQuery(id+"F5.opFillet","BLEND_EDGE",EDGE,{"blendedFrom":[makeQuery(id+"F3.opExtrude","CAP_EDGE",EDGE,{"disambiguationData":[OSD([subQ0])],"isStart":true}),makeQuery(id+"F3.opExtrude","CAP_FACE",FACE,{"disambiguationData":[OSD([subQ0,sQuery(id+"F2.wireOp",EDGE,"E3"),sQuery(id+"F2.wireOp",EDGE,"E4"),sQuery(id+"F2.wireOp",EDGE,"E12")])],"isStart":false})],"blendedInto":[makeQuery(id+"F3.opExtrude","CAP_FACE",FACE,{"disambiguationData":[OSD([subQ0,sQuery(id+"F2.wireOp",EDGE,"E3"),sQuery(id+"F2.wireOp",EDGE,"E4"),sQuery(id+"F2.wireOp",EDGE,"E12")])],"isStart":false})]});}
            var Q18;
            {var subQ0=sQuery(id+"F2.wireOp",EDGE,"E3");Q18=makeQuery(id+"F5.opFillet","BLEND_EDGE",EDGE,{"blendedFrom":[makeQuery(id+"F3.opExtrude","CAP_EDGE",EDGE,{"disambiguationData":[OSD([subQ0])],"isStart":true}),makeQuery(id+"F3.opExtrude","CAP_FACE",FACE,{"disambiguationData":[OSD([sQuery(id+"F2.wireOp",EDGE,"E2"),subQ0,sQuery(id+"F2.wireOp",EDGE,"E4"),sQuery(id+"F2.wireOp",EDGE,"E12")])],"isStart":false})],"blendedInto":[makeQuery(id+"F3.opExtrude","CAP_FACE",FACE,{"disambiguationData":[OSD([sQuery(id+"F2.wireOp",EDGE,"E2"),subQ0,sQuery(id+"F2.wireOp",EDGE,"E4"),sQuery(id+"F2.wireOp",EDGE,"E12")])],"isStart":false})]});}
            var Q19;
            {var subQ0=sQuery(id+"F2.wireOp",EDGE,"E12");Q19=makeQuery(id+"F6.opChamfer","BLEND_EDGE",EDGE,{"blendedFrom":[makeQuery(id+"F3.opExtrude","CAP_EDGE",EDGE,{"disambiguationData":[OSD([subQ0])],"isStart":false}),makeQuery(id+"F3.opExtrude","CAP_FACE",FACE,{"disambiguationData":[OSD([sQuery(id+"F2.wireOp",EDGE,"E2"),sQuery(id+"F2.wireOp",EDGE,"E3"),sQuery(id+"F2.wireOp",EDGE,"E4"),subQ0])],"isStart":false})],"blendedInto":[makeQuery(id+"F3.opExtrude","CAP_FACE",FACE,{"disambiguationData":[OSD([sQuery(id+"F2.wireOp",EDGE,"E2"),sQuery(id+"F2.wireOp",EDGE,"E3"),sQuery(id+"F2.wireOp",EDGE,"E4"),subQ0])],"isStart":false})]});}
            var Q20;
            {var subQ0=sQuery(id+"F2.wireOp",EDGE,"E12");Q20=makeQuery(id+"F6.opChamfer","BLEND_EDGE",EDGE,{"blendedFrom":[makeQuery(id+"F3.opExtrude","CAP_EDGE",EDGE,{"disambiguationData":[OSD([subQ0])],"isStart":false}),makeQuery(id+"F3.opExtrude","CAP_FACE",FACE,{"disambiguationData":[OSD([sQuery(id+"F2.wireOp",EDGE,"E2"),sQuery(id+"F2.wireOp",EDGE,"E3"),sQuery(id+"F2.wireOp",EDGE,"E4"),subQ0])],"isStart":true})],"blendedInto":[makeQuery(id+"F3.opExtrude","CAP_FACE",FACE,{"disambiguationData":[OSD([sQuery(id+"F2.wireOp",EDGE,"E2"),sQuery(id+"F2.wireOp",EDGE,"E3"),sQuery(id+"F2.wireOp",EDGE,"E4"),subQ0])],"isStart":true})]});}
            fillet(context, id + "F31", {"entities" : qUnion([Q0, Q1, Q2, Q3, Q4, Q5, Q6, Q7, Q8, Q9, Q10, Q11, Q12, Q13, Q14, Q15, Q16, Q17, Q18, Q19, Q20]), "radius" : 0.8 * mm, "tangentPropagation" : true, "allowEdgeOverflow" : false});
        }
        {
            var Q0;
            Q0=makeQuery(id+"F27.boolean.opBoolean","INTERSECT",EDGE,{"derivedFrom":[makeQuery(id+"F11.opExtrude","CAP_FACE",FACE,{"disambiguationData":[OSD([sQuery(id+"F10.wireOp",EDGE,"E28"),sQuery(id+"F10.wireOp",EDGE,"E29"),sQuery(id+"F10.wireOp",EDGE,"E31.MirrorCS"),sQuery(id+"F10.wireOp",EDGE,"E32.MirrorCS")])],"isStart":false}),makeQuery(id+"F27.opRevolve","CAP_FACE",FACE,{"disambiguationData":[OSD([sQuery(id+"F24.wireOp",EDGE,"E61"),sQuery(id+"F24.wireOp",EDGE,"E62"),sQuery(id+"F24.wireOp",EDGE,"E64"),sQuery(id+"F24.wireOp",EDGE,"E65")])],"isStart":false})]});
            var Q1;
            Q1=makeQuery(id+"F27.boolean.opBoolean","INTERSECT",EDGE,{"derivedFrom":[makeQuery(id+"F11.opExtrude","CAP_FACE",FACE,{"disambiguationData":[OSD([sQuery(id+"F10.wireOp",EDGE,"E28"),sQuery(id+"F10.wireOp",EDGE,"E29"),sQuery(id+"F10.wireOp",EDGE,"E31.MirrorCS"),sQuery(id+"F10.wireOp",EDGE,"E32.MirrorCS")])],"isStart":false}),makeQuery(id+"F27.opRevolve","SWEPT_FACE",FACE,{"disambiguationData":[OSD([sQuery(id+"F24.wireOp",EDGE,"E61")])]})]});
            var Q2;
            Q2=makeQuery(id+"F27.boolean.opBoolean","INTERSECT",EDGE,{"derivedFrom":[makeQuery(id+"F11.opExtrude","CAP_FACE",FACE,{"disambiguationData":[OSD([sQuery(id+"F10.wireOp",EDGE,"E28"),sQuery(id+"F10.wireOp",EDGE,"E29"),sQuery(id+"F10.wireOp",EDGE,"E31.MirrorCS"),sQuery(id+"F10.wireOp",EDGE,"E32.MirrorCS")])],"isStart":false}),makeQuery(id+"F27.opRevolve","CAP_FACE",FACE,{"disambiguationData":[OSD([sQuery(id+"F24.wireOp",EDGE,"E61"),sQuery(id+"F24.wireOp",EDGE,"E62"),sQuery(id+"F24.wireOp",EDGE,"E64"),sQuery(id+"F24.wireOp",EDGE,"E65")])],"isStart":true})]});
            fillet(context, id + "F32", {"entities" : qUnion([Q0, Q1, Q2]), "radius" : 1.27 * mm, "tangentPropagation" : true, "allowEdgeOverflow" : false});
        }
        {
            var Q0;
            Q0=makeQuery(id+"F27.boolean.opBoolean","INTERSECT",EDGE,{"derivedFrom":[makeQuery(id+"F11.opExtrude","CAP_FACE",FACE,{"disambiguationData":[OSD([sQuery(id+"F10.wireOp",EDGE,"E28"),sQuery(id+"F10.wireOp",EDGE,"E29"),sQuery(id+"F10.wireOp",EDGE,"E31.MirrorCS"),sQuery(id+"F10.wireOp",EDGE,"E32.MirrorCS")])],"isStart":false}),makeQuery(id+"F27.opRevolve","SWEPT_FACE",FACE,{"disambiguationData":[OSD([sQuery(id+"F24.wireOp",EDGE,"E65")])]})]});
            var Q1;
            Q1=makeQuery(id+"F27.boolean.opBoolean","COPY",EDGE,{"derivedFrom":makeQuery(id+"F27.opRevolve","SWEPT_EDGE",EDGE,{"disambiguationData":[OSD([sQuery(id+"F24.wireOp",EDGE,"E61"),sQuery(id+"F24.wireOp",EDGE,"E65")])]})});
            var Q2;
            {var subQ0=sQuery(id+"F24.wireOp",EDGE,"E65");Q2=makeQuery(id+"F32.opFillet","BLEND_EDGE",EDGE,{"blendedFrom":[makeQuery(id+"F27.boolean.opBoolean","INTERSECT",EDGE,{"derivedFrom":[makeQuery(id+"F11.opExtrude","CAP_FACE",FACE,{"disambiguationData":[OSD([sQuery(id+"F10.wireOp",EDGE,"E28"),sQuery(id+"F10.wireOp",EDGE,"E29"),sQuery(id+"F10.wireOp",EDGE,"E31.MirrorCS"),sQuery(id+"F10.wireOp",EDGE,"E32.MirrorCS")])],"isStart":false}),makeQuery(id+"F27.opRevolve","CAP_FACE",FACE,{"disambiguationData":[OSD([sQuery(id+"F24.wireOp",EDGE,"E61"),sQuery(id+"F24.wireOp",EDGE,"E62"),sQuery(id+"F24.wireOp",EDGE,"E64"),subQ0])],"isStart":false})]}),makeQuery(id+"F27.boolean.opBoolean","COPY",FACE,{"derivedFrom":makeQuery(id+"F27.opRevolve","SWEPT_FACE",FACE,{"disambiguationData":[OSD([subQ0])]})})],"blendedInto":[makeQuery(id+"F27.boolean.opBoolean","COPY",FACE,{"derivedFrom":makeQuery(id+"F27.opRevolve","SWEPT_FACE",FACE,{"disambiguationData":[OSD([subQ0])]})})]});}
            var Q3;
            {var subQ0=makeQuery(id+"F11.opExtrude","CAP_FACE",FACE,{"disambiguationData":[OSD([sQuery(id+"F10.wireOp",EDGE,"E28"),sQuery(id+"F10.wireOp",EDGE,"E29"),sQuery(id+"F10.wireOp",EDGE,"E31.MirrorCS"),sQuery(id+"F10.wireOp",EDGE,"E32.MirrorCS")])],"isStart":false});var subQ1=sQuery(id+"F24.wireOp",EDGE,"E65");var subQ2=sQuery(id+"F24.wireOp",EDGE,"E64");var subQ3=sQuery(id+"F24.wireOp",EDGE,"E62");var subQ4=sQuery(id+"F24.wireOp",EDGE,"E61");var subQ5=makeQuery(id+"F27.opRevolve","CAP_FACE",FACE,{"disambiguationData":[OSD([subQ4,subQ3,subQ2,subQ1])],"isStart":false});Q3=makeQuery(id+"F32.opFillet","BLEND_EDGE",EDGE,{"blendedFrom":[makeQuery(id+"F27.boolean.opBoolean","INTERSECT",EDGE,{"derivedFrom":[subQ0,subQ5]}),makeQuery(id+"F27.boolean.opBoolean","COPY",FACE,{"disambiguationData":[TD([makeQuery(id+"F27.opRevolve","SWEPT_FACE",FACE,{"disambiguationData":[OSD([subQ1])]})])],"derivedFrom":makeQuery(id+"F27.opRevolve","SWEPT_FACE",FACE,{"disambiguationData":[OSD([subQ4])]})})],"blendedInto":[makeQuery(id+"F27.boolean.opBoolean","COPY",FACE,{"disambiguationData":[TD([makeQuery(id+"F27.opRevolve","SWEPT_FACE",FACE,{"disambiguationData":[OSD([subQ1])]})])],"derivedFrom":makeQuery(id+"F27.opRevolve","SWEPT_FACE",FACE,{"disambiguationData":[OSD([subQ4])]})})]});}
            var Q4;
            {var subQ0=sQuery(id+"F24.wireOp",EDGE,"E61");var subQ1=makeQuery(id+"F11.opExtrude","CAP_FACE",FACE,{"disambiguationData":[OSD([sQuery(id+"F10.wireOp",EDGE,"E28"),sQuery(id+"F10.wireOp",EDGE,"E29"),sQuery(id+"F10.wireOp",EDGE,"E31.MirrorCS"),sQuery(id+"F10.wireOp",EDGE,"E32.MirrorCS")])],"isStart":false});Q4=makeQuery(id+"F32.opFillet","BLEND_EDGE",EDGE,{"blendedFrom":[makeQuery(id+"F27.boolean.opBoolean","INTERSECT",EDGE,{"derivedFrom":[subQ1,makeQuery(id+"F27.opRevolve","CAP_FACE",FACE,{"disambiguationData":[OSD([subQ0,sQuery(id+"F24.wireOp",EDGE,"E62"),sQuery(id+"F24.wireOp",EDGE,"E64"),sQuery(id+"F24.wireOp",EDGE,"E65")])],"isStart":false})]}),makeQuery(id+"F27.boolean.opBoolean","INTERSECT",EDGE,{"derivedFrom":[subQ1,makeQuery(id+"F27.opRevolve","SWEPT_FACE",FACE,{"disambiguationData":[OSD([subQ0])]})]})],"blendedInto":[]});}
            var Q5;
            {var subQ0=sQuery(id+"F24.wireOp",EDGE,"E61");var subQ1=makeQuery(id+"F11.opExtrude","CAP_FACE",FACE,{"disambiguationData":[OSD([sQuery(id+"F10.wireOp",EDGE,"E28"),sQuery(id+"F10.wireOp",EDGE,"E29"),sQuery(id+"F10.wireOp",EDGE,"E31.MirrorCS"),sQuery(id+"F10.wireOp",EDGE,"E32.MirrorCS")])],"isStart":false});Q5=makeQuery(id+"F32.opFillet","BLEND_EDGE",EDGE,{"blendedFrom":[makeQuery(id+"F27.boolean.opBoolean","INTERSECT",EDGE,{"derivedFrom":[subQ1,makeQuery(id+"F27.opRevolve","CAP_FACE",FACE,{"disambiguationData":[OSD([subQ0,sQuery(id+"F24.wireOp",EDGE,"E62"),sQuery(id+"F24.wireOp",EDGE,"E64"),sQuery(id+"F24.wireOp",EDGE,"E65")])],"isStart":true})]}),makeQuery(id+"F27.boolean.opBoolean","INTERSECT",EDGE,{"derivedFrom":[subQ1,makeQuery(id+"F27.opRevolve","SWEPT_FACE",FACE,{"disambiguationData":[OSD([subQ0])]})]})],"blendedInto":[]});}
            var Q6;
            {var subQ0=makeQuery(id+"F11.opExtrude","CAP_FACE",FACE,{"disambiguationData":[OSD([sQuery(id+"F10.wireOp",EDGE,"E28"),sQuery(id+"F10.wireOp",EDGE,"E29"),sQuery(id+"F10.wireOp",EDGE,"E31.MirrorCS"),sQuery(id+"F10.wireOp",EDGE,"E32.MirrorCS")])],"isStart":false});var subQ1=sQuery(id+"F24.wireOp",EDGE,"E65");var subQ2=sQuery(id+"F24.wireOp",EDGE,"E64");var subQ3=sQuery(id+"F24.wireOp",EDGE,"E62");var subQ4=sQuery(id+"F24.wireOp",EDGE,"E61");var subQ5=makeQuery(id+"F27.opRevolve","CAP_FACE",FACE,{"disambiguationData":[OSD([subQ4,subQ3,subQ2,subQ1])],"isStart":true});Q6=makeQuery(id+"F32.opFillet","BLEND_EDGE",EDGE,{"blendedFrom":[makeQuery(id+"F27.boolean.opBoolean","INTERSECT",EDGE,{"derivedFrom":[subQ0,subQ5]}),makeQuery(id+"F27.boolean.opBoolean","COPY",FACE,{"disambiguationData":[TD([makeQuery(id+"F27.opRevolve","SWEPT_FACE",FACE,{"disambiguationData":[OSD([subQ1])]})])],"derivedFrom":makeQuery(id+"F27.opRevolve","SWEPT_FACE",FACE,{"disambiguationData":[OSD([subQ4])]})})],"blendedInto":[makeQuery(id+"F27.boolean.opBoolean","COPY",FACE,{"disambiguationData":[TD([makeQuery(id+"F27.opRevolve","SWEPT_FACE",FACE,{"disambiguationData":[OSD([subQ1])]})])],"derivedFrom":makeQuery(id+"F27.opRevolve","SWEPT_FACE",FACE,{"disambiguationData":[OSD([subQ4])]})})]});}
            var Q7;
            {var subQ0=sQuery(id+"F24.wireOp",EDGE,"E65");Q7=makeQuery(id+"F32.opFillet","BLEND_EDGE",EDGE,{"blendedFrom":[makeQuery(id+"F27.boolean.opBoolean","INTERSECT",EDGE,{"derivedFrom":[makeQuery(id+"F11.opExtrude","CAP_FACE",FACE,{"disambiguationData":[OSD([sQuery(id+"F10.wireOp",EDGE,"E28"),sQuery(id+"F10.wireOp",EDGE,"E29"),sQuery(id+"F10.wireOp",EDGE,"E31.MirrorCS"),sQuery(id+"F10.wireOp",EDGE,"E32.MirrorCS")])],"isStart":false}),makeQuery(id+"F27.opRevolve","CAP_FACE",FACE,{"disambiguationData":[OSD([sQuery(id+"F24.wireOp",EDGE,"E61"),sQuery(id+"F24.wireOp",EDGE,"E62"),sQuery(id+"F24.wireOp",EDGE,"E64"),subQ0])],"isStart":true})]}),makeQuery(id+"F27.boolean.opBoolean","COPY",FACE,{"derivedFrom":makeQuery(id+"F27.opRevolve","SWEPT_FACE",FACE,{"disambiguationData":[OSD([subQ0])]})})],"blendedInto":[makeQuery(id+"F27.boolean.opBoolean","COPY",FACE,{"derivedFrom":makeQuery(id+"F27.opRevolve","SWEPT_FACE",FACE,{"disambiguationData":[OSD([subQ0])]})})]});}
            fillet(context, id + "F33", {"entities" : qUnion([Q0, Q1, Q2, Q3, Q4, Q5, Q6, Q7]), "radius" : 0.13 * mm, "tangentPropagation" : true, "allowEdgeOverflow" : false});
        }
    });
